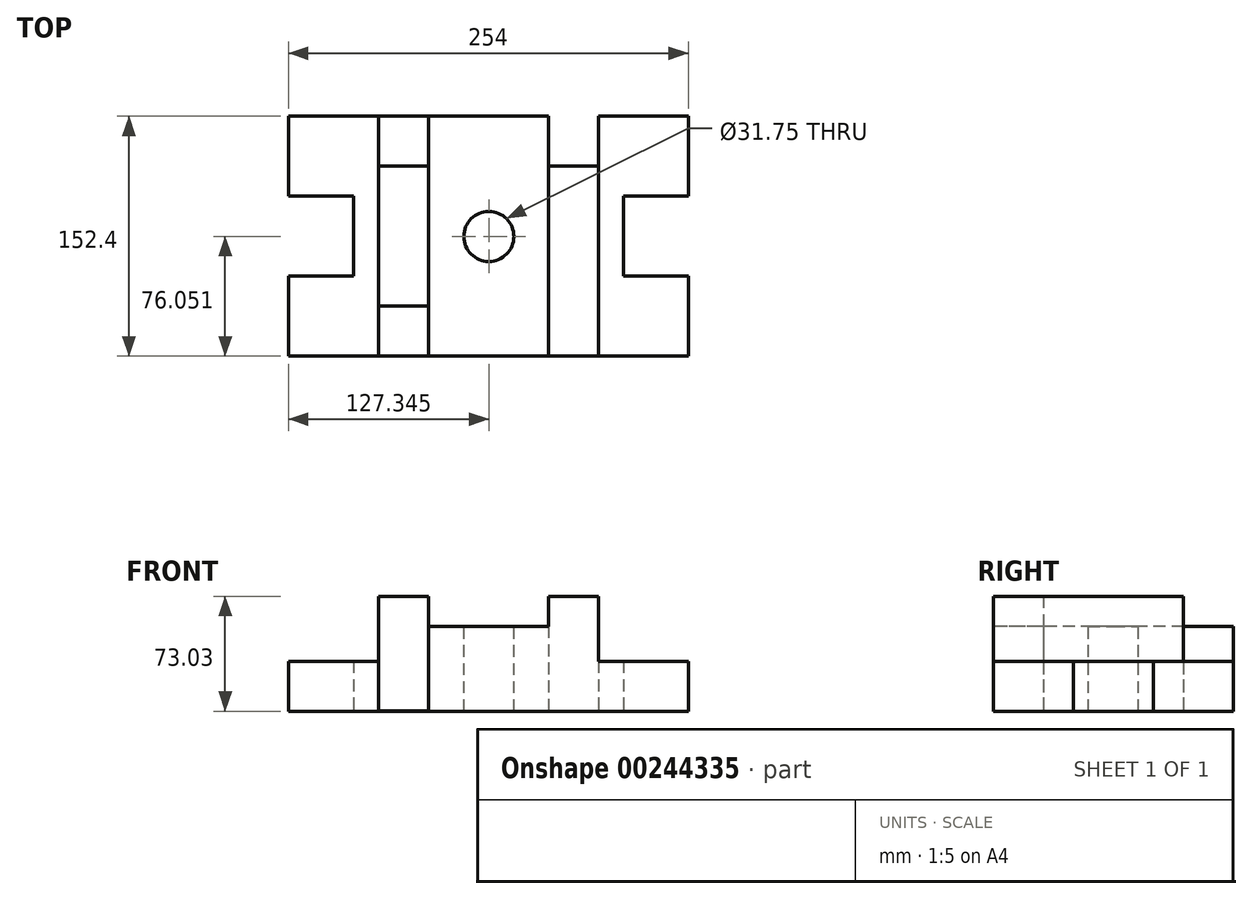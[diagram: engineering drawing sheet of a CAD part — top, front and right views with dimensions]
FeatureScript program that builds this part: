
annotation { "Feature Type Name" : "Feature", "Feature Type Description" : "" }
export const myFeature = defineFeature(function(context is Context, id is Id, definition is map)
    precondition{}
    {
        {
            var Q0;
            Q0=qCreatedBy(makeId("Top.planeOp"),FACE);
            var sketch = newSketch(context, id + "F0", { "sketchPlane" : qUnion([Q0])});
            skLineSegment(sketch, "E0", {"start": v(57.15, -45.34) * mm, "end": v(57.15, 5.46) * mm});
            skLineSegment(sketch, "E1", {"start": v(57.15, 5.46) * mm, "end": v(15.87, 5.46) * mm});
            skLineSegment(sketch, "E2", {"start": v(15.87, 5.46) * mm, "end": v(15.87, 56.26) * mm});
            skLineSegment(sketch, "E3", {"start": v(15.87, 56.26) * mm, "end": v(57.15, 56.26) * mm});
            skLineSegment(sketch, "E4", {"start": v(57.15, 56.26) * mm, "end": v(57.15, 107.06) * mm});
            skLineSegment(sketch, "E5", {"start": v(57.15, -45.34) * mm, "end": v(11.11, -45.34) * mm});
            skLineSegment(sketch, "E6", {"start": v(11.11, -45.34) * mm, "end": v(-31.75, -45.34) * mm});
            skLineSegment(sketch, "E7", {"start": v(-31.75, 107.06) * mm, "end": v(15.87, 107.06) * mm});
            skLineSegment(sketch, "E8", {"start": v(15.87, 107.06) * mm, "end": v(57.15, 107.06) * mm});
            skLineSegment(sketch, "E9", {"start": v(0, 107.06) * mm, "end": v(-31.75, 107.06) * mm});
            skLineSegment(sketch, "E10", {"start": v(0, -45.34) * mm, "end": v(-31.75, -45.34) * mm});
            skLineSegment(sketch, "E11", {"start": v(-31.75, 107.06) * mm, "end": v(-31.75, -45.34) * mm});
            skLineSegment(sketch, "E12", {"start": v(-31.75, -45.34) * mm, "end": v(-31.75, 0) * mm});
            skLineSegment(sketch, "E13", {"start": v(0, 107.06) * mm, "end": v(0, -45.34) * mm});
            skLineSegment(sketch, "E14", {"start": v(-31.75, -45.34) * mm, "end": v(-31.75, -22.67) * mm});
            skLineSegment(sketch, "E15", {"start": v(-31.75, -45.34) * mm, "end": v(-31.75, -13.6) * mm});
            skLineSegment(sketch, "E16", {"start": v(-31.75, -13.6) * mm, "end": v(0, -13.6) * mm});
            skLineSegment(sketch, "E17", {"start": v(-31.75, 107.06) * mm, "end": v(-31.75, 75.3) * mm});
            skLineSegment(sketch, "E18", {"start": v(-31.75, 75.3) * mm, "end": v(0, 75.3) * mm});
            skLineSegment(sketch, "E19", {"start": v(-31.75, 107.06) * mm, "end": v(-69.85, 107.06) * mm});
            skLineSegment(sketch, "E20", {"start": v(-31.75, -45.34) * mm, "end": v(-69.85, -45.34) * mm});
            skLineSegment(sketch, "E21", {"start": v(-69.85, 107.06) * mm, "end": v(-69.85, -45.34) * mm});
            skLineSegment(sketch, "E22.MirrorCS", {"start": v(-107.95, 107.06) * mm, "end": v(-69.85, 107.06) * mm});
            skLineSegment(sketch, "E23.MirrorCS", {"start": v(-107.95, -45.34) * mm, "end": v(-69.85, -45.34) * mm});
            skLineSegment(sketch, "E24.MirrorCS", {"start": v(-107.95, -45.34) * mm, "end": v(-107.95, 0) * mm});
            skLineSegment(sketch, "E25.MirrorCS", {"start": v(-139.7, 107.06) * mm, "end": v(-139.7, -45.34) * mm});
            skLineSegment(sketch, "E26.MirrorCS", {"start": v(-107.95, 107.06) * mm, "end": v(-107.95, -45.34) * mm});
            skLineSegment(sketch, "E27.MirrorCS", {"start": v(-107.95, 75.3) * mm, "end": v(-139.7, 75.3) * mm});
            skLineSegment(sketch, "E28.MirrorCS", {"start": v(-107.95, -13.6) * mm, "end": v(-139.7, -13.6) * mm});
            skLineSegment(sketch, "E29.MirrorCS", {"start": v(-139.7, 107.06) * mm, "end": v(-107.95, 107.06) * mm});
            skLineSegment(sketch, "E30.MirrorCS", {"start": v(-196.85, -45.34) * mm, "end": v(-150.81, -45.34) * mm});
            skLineSegment(sketch, "E31.MirrorCS", {"start": v(-150.81, -45.34) * mm, "end": v(-107.95, -45.34) * mm});
            skLineSegment(sketch, "E32.MirrorCS", {"start": v(-196.85, -45.34) * mm, "end": v(-196.85, 5.46) * mm});
            skLineSegment(sketch, "E33.MirrorCS", {"start": v(-196.85, 56.26) * mm, "end": v(-196.85, 107.06) * mm});
            skLineSegment(sketch, "E34.MirrorCS", {"start": v(-155.58, 107.06) * mm, "end": v(-196.85, 107.06) * mm});
            skLineSegment(sketch, "E35.MirrorCS", {"start": v(-107.95, 107.06) * mm, "end": v(-155.58, 107.06) * mm});
            skLineSegment(sketch, "E36.MirrorCS", {"start": v(-155.57, 5.46) * mm, "end": v(-155.57, 56.26) * mm});
            skLineSegment(sketch, "E37.MirrorCS", {"start": v(-196.85, 5.46) * mm, "end": v(-155.57, 5.46) * mm});
            skLineSegment(sketch, "E38.MirrorCS", {"start": v(-155.57, 56.26) * mm, "end": v(-196.85, 56.26) * mm});
            skSolve(sketch);
        }
        {
            var Q0;
            Q0=makeQuery(id+"F0.imprint","IMPRINT",FACE,{"disambiguationData":[TD([[makeQuery(id+"F0.imprint","IMPRINT",EDGE,{"derivedFrom":sQuery(id+"F0.wireOp",EDGE,"E0")}),1.0]])]});
            var Q1;
            {var subQ4=sQuery(id+"F0.wireOp",EDGE,"E30.MirrorCS");Q1=makeQuery(id+"F0.imprint","IMPRINT",FACE,{"disambiguationData":[TD([[makeQuery(id+"F0.imprint","IMPRINT",EDGE,{"derivedFrom":subQ4}),1.0]])]});}
            extrude(context, id + "F1", {"entities" : qUnion([Q0, Q1]), "depth" : 31.75 * mm});
        }
        {
            var Q0;
            {var subQ3=sQuery(id+"F0.wireOp",EDGE,"E10");Q0=makeQuery(id+"F0.imprint","IMPRINT",FACE,{"disambiguationData":[TD([[makeQuery(id+"F0.imprint","IMPRINT",EDGE,{"derivedFrom":subQ3}),-1.0]])]});}
            var Q1;
            {var subQ3=sQuery(id+"F0.wireOp",EDGE,"E28.MirrorCS");Q1=makeQuery(id+"F0.imprint","IMPRINT",FACE,{"disambiguationData":[TD([[makeQuery(id+"F0.imprint","IMPRINT",EDGE,{"derivedFrom":subQ3}),1.0]])]});}
            var Q2;
            {var subQ3=sQuery(id+"F0.wireOp",EDGE,"E27.MirrorCS");Q2=makeQuery(id+"F0.imprint","IMPRINT",FACE,{"disambiguationData":[TD([[makeQuery(id+"F0.imprint","IMPRINT",EDGE,{"derivedFrom":subQ3}),-1.0]])]});}
            var Q3;
            {var subQ0=sQuery(id+"F0.wireOp",EDGE,"E9");Q3=makeQuery(id+"F0.imprint","IMPRINT",FACE,{"disambiguationData":[TD([[makeQuery(id+"F0.imprint","IMPRINT",EDGE,{"derivedFrom":subQ0}),1.0]])]});}
            extrude(context, id + "F2", {"entities" : qUnion([Q0, Q1, Q2, Q3]), "operationType" : NewBodyOperationType.ADD, "depth" : 29 / 203.2 * mm});
        }
        {
            var Q0;
            Q0=makeQuery(id+"F0.imprint","IMPRINT",FACE,{"disambiguationData":[TD([[makeQuery(id+"F0.imprint","IMPRINT",EDGE,{"derivedFrom":sQuery(id+"F0.wireOp",EDGE,"E11")}),1.0]])]});
            var Q1;
            {var subQ0=sQuery(id+"F0.wireOp",EDGE,"521ebe99-49bb-44c1-a3a0-b59e7b7f198b0.MirrorCS");Q1=makeQuery(id+"F0.imprint","IMPRINT",FACE,{"disambiguationData":[TD([[makeQuery(id+"F0.imprint","IMPRINT",EDGE,{"derivedFrom":subQ0}),-1.0]])]});}
            var Q2;
            {var subQ0=sQuery(id+"F0.wireOp",EDGE,"E27.MirrorCS");Q2=makeQuery(id+"F0.imprint","IMPRINT",FACE,{"disambiguationData":[TD([[makeQuery(id+"F0.imprint","IMPRINT",EDGE,{"derivedFrom":subQ0}),1.0]])]});}
            extrude(context, id + "F3", {"entities" : qUnion([Q0, Q1, Q2]), "operationType" : NewBodyOperationType.ADD, "depth" : 73.02 * mm});
        }
        {
            var Q0;
            Q0=makeQuery(id+"F0.imprint","IMPRINT",FACE,{"disambiguationData":[TD([[makeQuery(id+"F0.imprint","IMPRINT",EDGE,{"derivedFrom":sQuery(id+"F0.wireOp",EDGE,"E21")}),-1.0]])]});
            var Q1;
            Q1=makeQuery(id+"F0.imprint","IMPRINT",FACE,{"disambiguationData":[TD([[makeQuery(id+"F0.imprint","IMPRINT",EDGE,{"derivedFrom":sQuery(id+"F0.wireOp",EDGE,"E11")}),-1.0]])]});
            extrude(context, id + "F4", {"entities" : qUnion([Q0, Q1]), "operationType" : NewBodyOperationType.ADD, "depth" : 53.97 * mm});
        }
        {
            var Q0;
            Q0=makeQuery(id+"F4.opExtrude","CAP_FACE",FACE,{"disambiguationData":[OSD([sQuery(id+"F0.wireOp",EDGE,"E6"),sQuery(id+"F0.wireOp",EDGE,"E7"),sQuery(id+"F0.wireOp",EDGE,"E11"),sQuery(id+"F0.wireOp",EDGE,"E12"),sQuery(id+"F0.wireOp",EDGE,"E15"),sQuery(id+"F0.wireOp",EDGE,"E17"),sQuery(id+"F0.wireOp",EDGE,"fcf5e975-8678-471d-8784-8bba8bb37cbb0.MirrorCS"),sQuery(id+"F0.wireOp",EDGE,"5d222d3b-47d3-40bb-952f-0f579ac0d8290.MirrorCS"),sQuery(id+"F0.wireOp",EDGE,"762ab704-d818-4e66-ae8d-3d58f55a7fdc0.MirrorCS")])],"isStart":false});
            var sketch = newSketch(context, id + "F5", { "sketchPlane" : qUnion([Q0])});
            skCircle(sketch, "E39", {"center": v(-69.5, 30.71) * mm, "radius": 15.88 * mm});
            skPoint(sketch, "E40.orphan", {"position": v(-72.67, -45.34) * mm});
            skSolve(sketch);
        }
        {
            var Q0;
            Q0=makeQuery(id+"F5.imprint","IMPRINT",FACE,{"disambiguationData":[TD([[makeQuery(id+"F5.imprint","IMPRINT",EDGE,{"derivedFrom":sQuery(id+"F5.wireOp",EDGE,"E39")}),1.0]])]});
            extrude(context, id + "F6", {"entities" : qUnion([Q0]), "operationType" : NewBodyOperationType.REMOVE, "oppositeDirection" : true, "depth" : 53.97 * mm});
        }
    });
